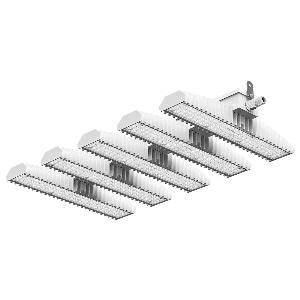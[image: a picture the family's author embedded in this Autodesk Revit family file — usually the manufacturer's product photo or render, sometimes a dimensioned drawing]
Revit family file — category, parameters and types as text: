
# Revit family: 3f_filippi_-_3f_lem_ho_ampio_3f_filippi_-_58976_-_3f_lem_5_ho_led_350_dali_cr_ampio
name_source: partatom
category: Lighting Fixtures
units: mm (PartAtom-declared; Revit-internal decimal feet)

## family parameters
Cut with Voids When Loaded = No
Host = Face
Light Source = No
Part Type = Normal
Room Calculation Point = No
Round Connector Dimension = Use Diameter
Shared = No

## types (1)
- 3F Filippi - 3F LEM HO Ampio (1 x LED, 56516 lm, 345 W, 4000 K)
    Apparent Load = 345 VA
    Approval mark = CE
    CIE Flux Codes = 60 92 99 100 100
    Color Rendering = 80
    Color Temperature = 4000 K
    Control Gear = Electronic transformer
    Default Elevation = 1800 mm
    Description = Industrial luminaire with high light output and high luminous efficiency designed with the most innovative technologies for environments with temperature up to 55°C.

ILLUMINOTECHNICAL
Luminous efficiency 100% (DLOR 100%, ULOR 0%).
Initial luminous flux of the luminaire 56516 lm.
Direct symmetric wide distribution: the illuminated area has a rectangular shape.
Installation Interdistance Transv.D = 1.58 x hu - Long.D = 1.45 x hu.
Tabular UGR (CIE 117 - 4H-8H; S=0.25H; 70/50/20): RUG 24.2 - 25.2.
Beam angle: 93° - 99°.
Luminous efficacy 164 lm/W.
Lifetime (L93/B10): 30000 h. (tq+25°C)
Lifetime (L90/B10): 50000 h. (tq+25°C)
Lifetime (L85/B10): 80000 h. (tq+25°C)
Lifetime (L80/B10): 100000 h. (tq+25°C)
Lifetime (L85/B10): 50000 h. (tq+55°C)
Sudden decreased luminous flux after 50000 hours: 0% (C0).
Photobiological safety in compliance with IEC/TR 62778: RG0 risk exempt, (IEC 62471).
In compliance with IEC/EN 62722-2-1 - IEC/EN 62717 standards.

SOURCE
5 Mid-Power linear LED modules 70W/840.
Energy efficiency class (UE 2019/2020 - UE 2019/2015): C.
CIE 13.3 Colour rendering index: CRI >80 (R9 <50%).
IES TM-30 Fidelity Index: Rf = 84 Rg = 95.
CCT nominal colour temperature 4000 K.
Colour initial tolerance (MacAdam): SDCM 3.

MECHANICAL
Passive modular heatsinks in die-casted aluminium, painted in white colour.
To optimize the thermal management of the LED module, the heatsinks are oversized and provided with self-cleaning of cooling fins.
Wiring body in aluminium and galvanised steel anchored solidly to the sinks and thermally separated.
3F Lens lenses with high luminous efficiency, transparent methacrylate (PMMA), fixed to the LED modules.
Fixing brackets in stainless steel.
Luminaire with limited surface temperature. - D - (EN 60598-2-24)
Dimensions: 952x542 mm, height 129 mm. Weight 21.705 kg.
IP65 protection degree.
Mechanical strength to impacts IK06 (1 joule).
Glow-wire test resistance 650°C.

ELECTRICAL
Halogen Free DALI-2 DATI (Parts 251, 252, 253), PUSH-DIM, electronic wiring 230V-50/60Hz, power factor 0.97 at full load, THD <25%, constant output current, class I, 3 driver, 3 DALI addresses.
Power of the luminaire 345 W.
ENEC - CE.
SAFE FLICKER: PstLM=<1 and SVM=<0.4 (IEC TR 61547-1 and IEC TR 63158), to ensure a more comfortable and safe light.
Luminaire compliant with EN 60598-2-22 for power supply from a centralised emergency system CPSS (Central Power Supply System), not incorporated in the luminaire - high risk areas excluded. The default power and flux are 100% in AC and 15% in DC.
Ambient temperature from -30°C to +55°C.
Temperature class T6 max 85°C.
Quick connection via M25 5P connector with 9-13 mm tightening range.
Power unit positioned on a separate compartment by the LED module to ensure optimum temperatures of cabling components, to be inspectable and maintainable.
Relative humidity UR: <85%.

INSTALLATION
Ceiling / Suspended / Wall.
All accessories dedicated to this product are available on the Catalog and on our website www.3F-Filippi.com.

APPLICATIONS
In commercial environments, exhibition and industrial areas, stores, open areas.
Environments in which it is necessary a total protection against falling fragments (eg environments with foodstuffs or machines with moving parts or with extreme temperature changes), use luminaires with polycarbonate lenses.

LIGHT MANAGEMENT
Recommended minimum setting: 10%.
The luminaire, equipped with (DALI-2 DATI) driver, can be controlled manually with 3F Easy Dim technology or automatically/manually with wired or wireless DALI/D2D control systems.
The D2D driver guarantees interoperability with other devices with the same certification by making the following information available:
Device Data (Part 251), Energy Report (Part 252), Diagnosis & Maintenance (Part 253).
In electrical systems without a regulation system (manual or automatic) and DALI bus, a suitable jumper must be made on the DA-DA terminals of the appliance.

WARNING
Fixture not suitable for cold stores with an ambient temperature <0°C and/or relative humidity >85%.
Luminaire designed for disposal/recycling at end-of-life.
Replaceable (LED only) light source by a professional. Replaceable control gear by a professional.
    Height = 129 mm
    Lamp = 1 x LED
    Lamp Light Flux = 56516 lm
    Lamp Power = 345 W
    Lamp count = 1
    Length = 952 mm
    Lifetime = 50000 h
    Luminous efficacy = 164 lm/W
    Manufacturer = 3F Filippi
    ModVariant = No
    Model = 3F Filippi - 58976 - 3F LEM 5 HO LED 350 DALI CR AMPIO
    Mounting Place = Ceiling
    Mounting Type = Pendant
    Number of Poles = 1
    OnlyDefault = Yes
    Power Factor = 1
    Product Name = 3F Filippi - 3F LEM HO Ampio
    Product group = pendant luminaire
    ProductGroupID = 9
    Protection Class = Protection class I
    Protection Degree = IP 65
    RLX_Detail_Level = 1
    RLX_Emergency_Light_Flux = 0 lm
    RLX_Emergency_Type = 0
    RLX_Emergency_Type_DB = No
    RlxData = <blob elided: 134761 chars, md5=a8aa2141>
    Socket = socket
    Standby Power = 0 W
    System Light Flux = 56516 lm
    System Power = 345 W
    Type Comments = Product without accessories
    Type Image = 3f_filippi_-_lem_5.jpg
    URL = http://relux.com
    VarID = ---
    Voltage = 0 V
    Weight = 0.00 kg
    Width = 542 mm

## geometry (parser evidence)
native form markers: Blend x4, Sweep x14
no freeform markers — native parametric forms only
